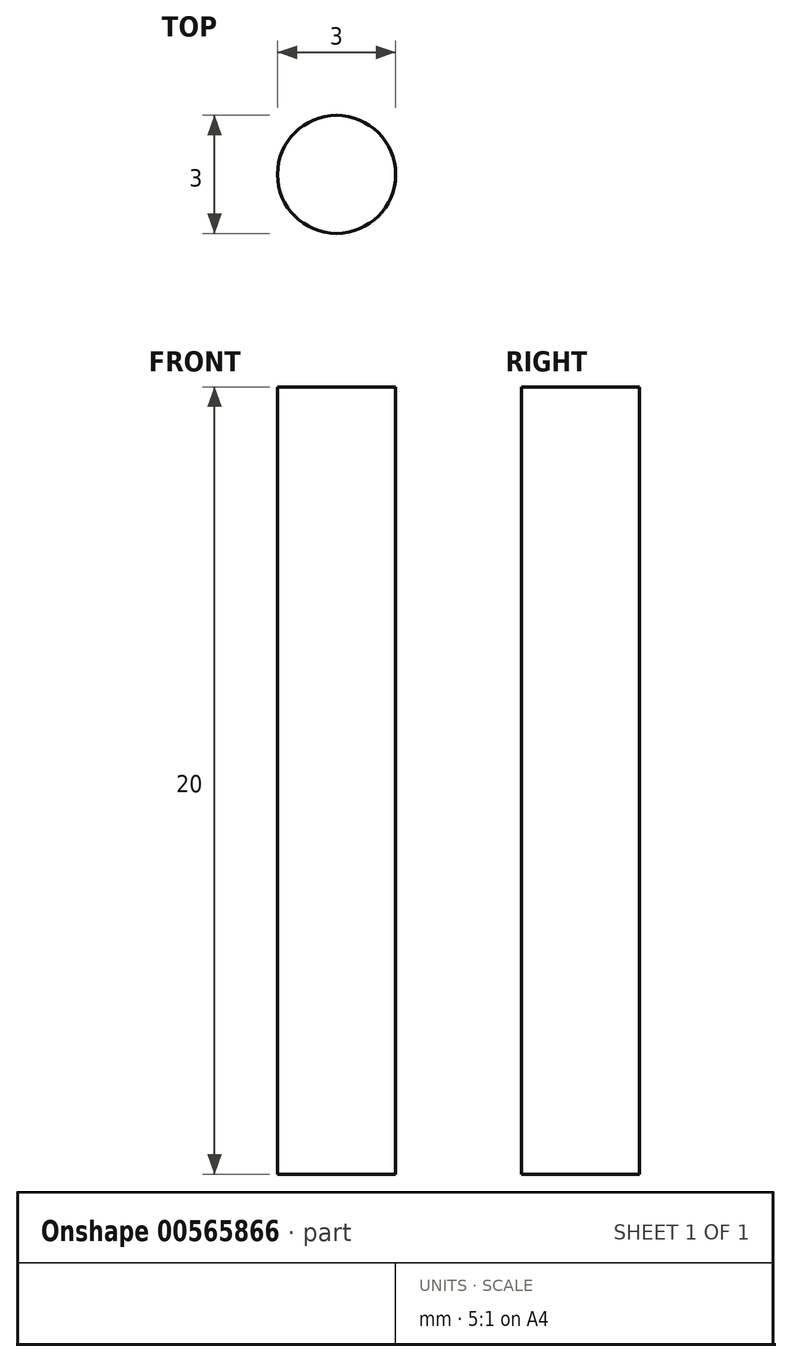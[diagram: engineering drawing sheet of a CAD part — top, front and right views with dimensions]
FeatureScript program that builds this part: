
annotation { "Feature Type Name" : "Feature", "Feature Type Description" : "" }
export const myFeature = defineFeature(function(context is Context, id is Id, definition is map)
    precondition{}
    {
        {
            var Q0;
            Q0=qCreatedBy(makeId("Top.planeOp"),FACE);
            var sketch = newSketch(context, id + "F0", { "sketchPlane" : qUnion([Q0])});
            skCircle(sketch, "E0", {"center": v(0, 0) * mm, "radius": 1.5 * mm});
            skSolve(sketch);
        }
        {
            var Q0;
            Q0=makeQuery(id+"F0.imprint","IMPRINT",FACE,{"disambiguationData":[TD([[makeQuery(id+"F0.imprint","IMPRINT",EDGE,{"derivedFrom":sQuery(id+"F0.wireOp",EDGE,"E0")}),1.0]])]});
            extrude(context, id + "F1", {"entities" : qUnion([Q0]), "depth" : 20 * mm, "offsetDistance" : 25 * mm});
        }
    });
